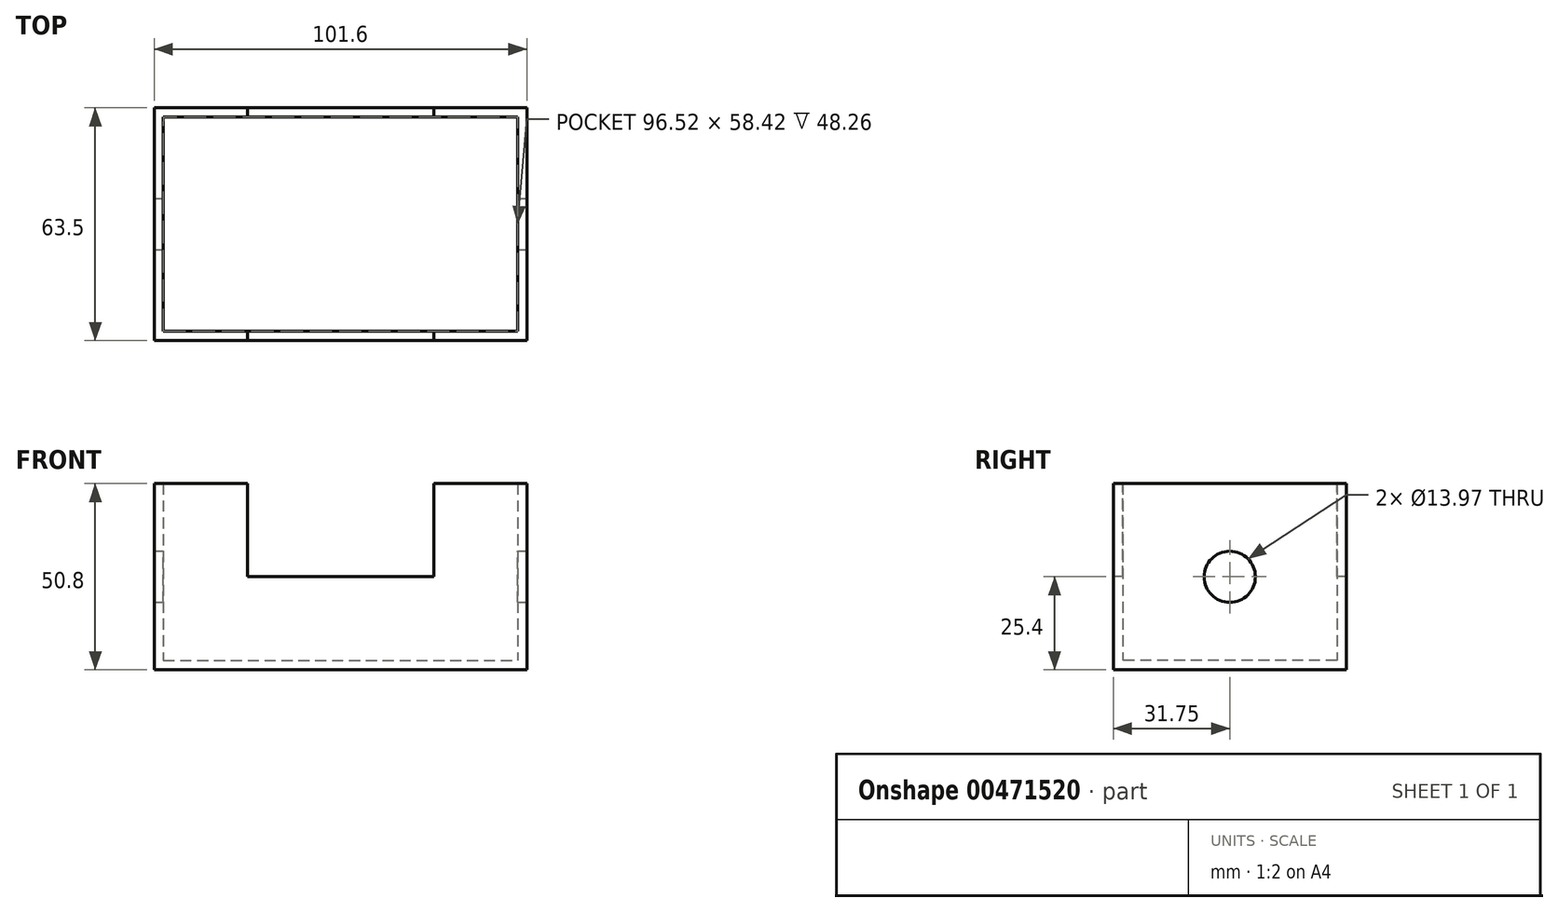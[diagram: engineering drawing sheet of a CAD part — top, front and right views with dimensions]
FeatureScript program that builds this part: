
annotation { "Feature Type Name" : "Feature", "Feature Type Description" : "" }
export const myFeature = defineFeature(function(context is Context, id is Id, definition is map)
    precondition{}
    {
        {
            var Q0;
            Q0=qCreatedBy(makeId("Top.planeOp"),FACE);
            var sketch = newSketch(context, id + "F0", { "sketchPlane" : qUnion([Q0])});
            skLineSegment(sketch, "E0.bottom", {"start": v(-50.8, 31.75) * mm, "end": v(50.8, 31.75) * mm});
            skLineSegment(sketch, "E0.top", {"start": v(-50.8, -31.75) * mm, "end": v(50.8, -31.75) * mm});
            skLineSegment(sketch, "E0.left", {"start": v(-50.8, 31.75) * mm, "end": v(-50.8, -31.75) * mm});
            skLineSegment(sketch, "E0.right", {"start": v(50.8, 31.75) * mm, "end": v(50.8, -31.75) * mm});
            skSolve(sketch);
        }
        {
            var Q0;
            Q0=makeQuery(id+"F0.imprint","IMPRINT",FACE,{"disambiguationData":[TD([[makeQuery(id+"F0.imprint","IMPRINT",EDGE,{"derivedFrom":sQuery(id+"F0.wireOp",EDGE,"E0.bottom")}),-1.0]])]});
            extrude(context, id + "F1", {"entities" : qUnion([Q0]), "depth" : 50.8 * mm});
        }
        {
            var Q0;
            Q0=makeQuery(id+"F1.opExtrude","CAP_FACE",FACE,{"disambiguationData":[OSD([sQuery(id+"F0.wireOp",EDGE,"E0.bottom"),sQuery(id+"F0.wireOp",EDGE,"E0.top"),sQuery(id+"F0.wireOp",EDGE,"E0.left"),sQuery(id+"F0.wireOp",EDGE,"E0.right")])],"isStart":false});
            shell(context, id + "F2", {"entities" : qUnion([Q0]), "thickness" : 2.54 * mm});
        }
        {
            var Q0;
            Q0=makeQuery(id+"F1.opExtrude","SWEPT_FACE",FACE,{"disambiguationData":[OSD([sQuery(id+"F0.wireOp",EDGE,"E0.right")])]});
            var sketch = newSketch(context, id + "F3", { "sketchPlane" : qUnion([Q0])});
            skCircle(sketch, "E1", {"center": v(0, 25.4) * mm, "radius": 6.99 * mm});
            skLineSegment(sketch, "E2", {"start": v(-19.56, 25.4) * mm, "end": v(18, 25.4) * mm, "construction": true});
            skSolve(sketch);
        }
        {
            var Q0;
            Q0 = qSketchRegion(id + "F3", true);
            extrude(context, id + "F4", {"entities" : qUnion([Q0]), "operationType" : NewBodyOperationType.REMOVE, "endBound" : BoundingType.THROUGH_ALL, "oppositeDirection" : true, "depth" : 25.4 * mm});
        }
        {
            var Q0;
            Q0=makeQuery(id+"F1.opExtrude","SWEPT_FACE",FACE,{"disambiguationData":[OSD([sQuery(id+"F0.wireOp",EDGE,"E0.top")])]});
            var sketch = newSketch(context, id + "F5", { "sketchPlane" : qUnion([Q0])});
            skLineSegment(sketch, "E3.bottom", {"start": v(-25.4, 50.8) * mm, "end": v(25.4, 50.8) * mm});
            skLineSegment(sketch, "E3.top", {"start": v(-25.4, 25.4) * mm, "end": v(25.4, 25.4) * mm});
            skLineSegment(sketch, "E3.left", {"start": v(-25.4, 50.8) * mm, "end": v(-25.4, 25.4) * mm});
            skLineSegment(sketch, "E3.right", {"start": v(25.4, 50.8) * mm, "end": v(25.4, 25.4) * mm});
            skSolve(sketch);
        }
        {
            var Q0;
            Q0=makeQuery(id+"F5.imprint","IMPRINT",FACE,{"disambiguationData":[TD([[makeQuery(id+"F5.imprint","IMPRINT",EDGE,{"derivedFrom":sQuery(id+"F5.wireOp",EDGE,"E3.bottom")}),-1.0]])]});
            extrude(context, id + "F6", {"entities" : qUnion([Q0]), "operationType" : NewBodyOperationType.REMOVE, "endBound" : BoundingType.THROUGH_ALL, "oppositeDirection" : true, "depth" : 25.4 * mm});
        }
    });
